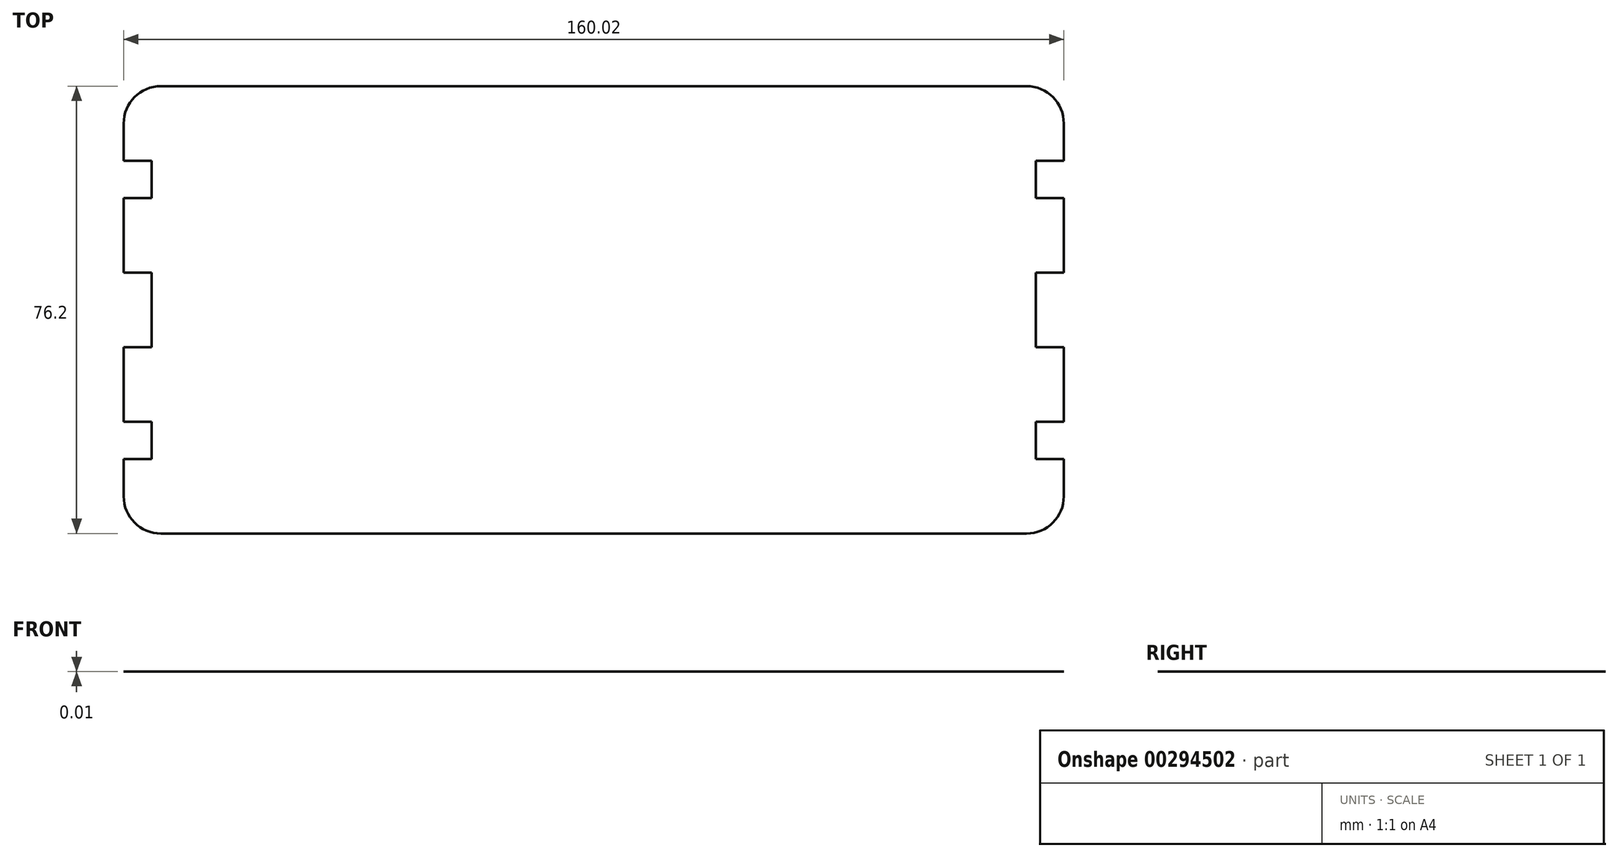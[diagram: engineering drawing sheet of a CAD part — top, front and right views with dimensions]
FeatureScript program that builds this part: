
annotation { "Feature Type Name" : "Feature", "Feature Type Description" : "" }
export const myFeature = defineFeature(function(context is Context, id is Id, definition is map)
    precondition{}
    {
        {
            var Q0;
            Q0=qCreatedBy(makeId("Top.planeOp"),FACE);
            var sketch = newSketch(context, id + "F0", { "sketchPlane" : qUnion([Q0])});
            skLineSegment(sketch, "E0.bottom", {"start": v(6.35, 0) * mm, "end": v(80, 0) * mm});
            skLineSegment(sketch, "E0.top", {"start": v(6.35, 76.2) * mm, "end": v(80, 76.2) * mm});
            skLineSegment(sketch, "E0.left", {"start": v(0, 6.35) * mm, "end": v(0, 12.7) * mm});
            skLineSegment(sketch, "E1", {"start": v(80.01, 76.2) * mm, "end": v(80.01, 0) * mm, "construction": true});
            skLineSegment(sketch, "E2.bottom", {"start": v(0, 44.45) * mm, "end": v(4.76, 44.45) * mm});
            skLineSegment(sketch, "E2.top", {"start": v(0, 31.75) * mm, "end": v(4.76, 31.75) * mm});
            skLineSegment(sketch, "E2.right", {"start": v(4.76, 44.45) * mm, "end": v(4.76, 31.75) * mm});
            skLineSegment(sketch, "E3.bottom", {"start": v(0, 19.05) * mm, "end": v(4.76, 19.05) * mm});
            skLineSegment(sketch, "E3.top", {"start": v(0, 12.7) * mm, "end": v(4.76, 12.7) * mm});
            skLineSegment(sketch, "E3.right", {"start": v(4.76, 19.05) * mm, "end": v(4.76, 12.7) * mm});
            skLineSegment(sketch, "E4.bottom", {"start": v(0, 57.15) * mm, "end": v(4.76, 57.15) * mm});
            skLineSegment(sketch, "E4.top", {"start": v(0, 63.5) * mm, "end": v(4.76, 63.5) * mm});
            skLineSegment(sketch, "E4.right", {"start": v(4.76, 57.15) * mm, "end": v(4.76, 63.5) * mm});
            skLineSegment(sketch, "E5.trimOffspring", {"start": v(0, 63.5) * mm, "end": v(0, 69.85) * mm});
            skLineSegment(sketch, "E6.trimOffspring", {"start": v(0, 44.45) * mm, "end": v(0, 57.15) * mm});
            skLineSegment(sketch, "E7.trimOffspring", {"start": v(0, 19.05) * mm, "end": v(0, 31.75) * mm});
            skLineSegment(sketch, "E8", {"start": v(4.76, 38.1) * mm, "end": v(80.01, 38.1) * mm, "construction": true});
            skPoint(sketch, "E9.visualSharp", {"position": v(0, 76.2) * mm});
            skArc(sketch, "E9.filletArc", {"start": v(6.35, 76.2) * mm, "mid": v(1.86, 74.34) * mm, "end": v(0, 69.85) * mm});
            skPoint(sketch, "E10.visualSharp", {"position": v(0, 0) * mm});
            skArc(sketch, "E10.filletArc", {"start": v(0, 6.35) * mm, "mid": v(1.86, 1.86) * mm, "end": v(6.35, 0) * mm});
            skPoint(sketch, "E0.right.end.orphan", {"position": v(160.02, 76.2) * mm});
            skPoint(sketch, "E11.orphan", {"position": v(160.02, 0) * mm});
            skLineSegment(sketch, "E12.MirrorCS", {"start": v(160.02, 31.75) * mm, "end": v(155.26, 31.75) * mm});
            skLineSegment(sketch, "E13.MirrorCS", {"start": v(160.02, 19.05) * mm, "end": v(155.26, 19.05) * mm});
            skLineSegment(sketch, "E14.MirrorCS", {"start": v(160.02, 44.45) * mm, "end": v(155.26, 44.45) * mm});
            skLineSegment(sketch, "E15.MirrorCS", {"start": v(160.02, 57.15) * mm, "end": v(155.26, 57.15) * mm});
            skLineSegment(sketch, "E16.MirrorCS", {"start": v(155.26, 19.05) * mm, "end": v(155.26, 12.7) * mm});
            skArc(sketch, "E17.MirrorCS", {"start": v(153.67, 76.2) * mm, "mid": v(158.16, 74.34) * mm, "end": v(160.02, 69.85) * mm});
            skLineSegment(sketch, "E18.MirrorCS", {"start": v(155.26, 57.15) * mm, "end": v(155.26, 63.5) * mm});
            skLineSegment(sketch, "E19.MirrorCS", {"start": v(153.67, 76.2) * mm, "end": v(80, 76.2) * mm});
            skLineSegment(sketch, "E20.MirrorCS", {"start": v(155.26, 44.45) * mm, "end": v(155.26, 31.75) * mm});
            skLineSegment(sketch, "E21.MirrorCS", {"start": v(153.67, 0) * mm, "end": v(80, 0) * mm});
            skLineSegment(sketch, "E22.MirrorCS", {"start": v(160.02, 63.5) * mm, "end": v(160.02, 69.85) * mm});
            skLineSegment(sketch, "E23.MirrorCS", {"start": v(155.26, 38.1) * mm, "end": v(80.01, 38.1) * mm, "construction": true});
            skLineSegment(sketch, "E24.MirrorCS", {"start": v(160.02, 12.7) * mm, "end": v(155.26, 12.7) * mm});
            skLineSegment(sketch, "E25.MirrorCS", {"start": v(160.02, 6.35) * mm, "end": v(160.02, 12.7) * mm});
            skArc(sketch, "E26.MirrorCS", {"start": v(160.02, 6.35) * mm, "mid": v(158.16, 1.86) * mm, "end": v(153.67, 0) * mm});
            skLineSegment(sketch, "E27.MirrorCS", {"start": v(160.02, 19.05) * mm, "end": v(160.02, 31.75) * mm});
            skLineSegment(sketch, "E28.MirrorCS", {"start": v(160.02, 63.5) * mm, "end": v(155.26, 63.5) * mm});
            skLineSegment(sketch, "E29.MirrorCS", {"start": v(160.02, 44.45) * mm, "end": v(160.02, 57.15) * mm});
            skSolve(sketch);
        }
        {
            var Q0;
            Q0=makeQuery(id+"F0.imprint","IMPRINT",FACE,{"disambiguationData":[TD([[makeQuery(id+"F0.imprint","IMPRINT",EDGE,{"derivedFrom":sQuery(id+"F0.wireOp",EDGE,"uaa8uD0J-ltQg-69X9-7cON-IVpzLo8zILYB.bottom")}),1.0]])]});
            var Q1;
            Q1=makeQuery(id+"F0.imprint","IMPRINT",FACE,{"disambiguationData":[TD([[makeQuery(id+"F0.imprint","IMPRINT",EDGE,{"derivedFrom":sQuery(id+"F0.wireOp",EDGE,"E0.bottom")}),1.0]])]});
            extrude(context, id + "F1", {"entities" : qUnion([Q0, Q1]), "depth" : 3 / 406.4 * mm});
        }
    });
